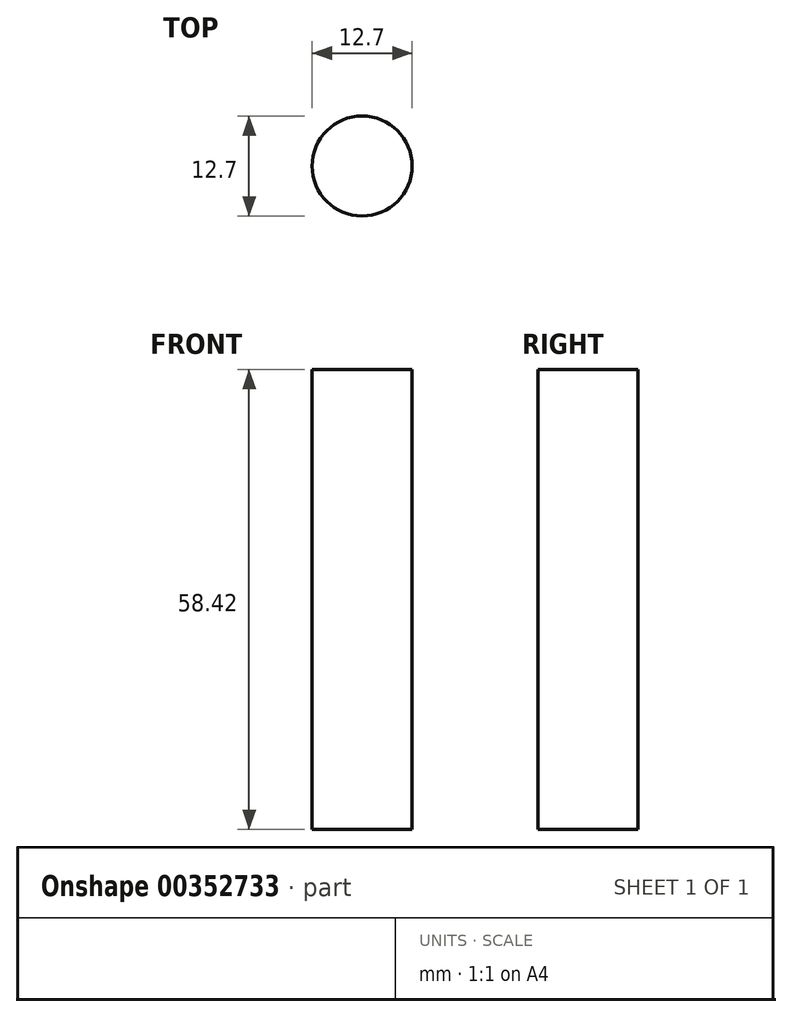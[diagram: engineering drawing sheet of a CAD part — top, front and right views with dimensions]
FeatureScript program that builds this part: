
annotation { "Feature Type Name" : "Feature", "Feature Type Description" : "" }
export const myFeature = defineFeature(function(context is Context, id is Id, definition is map)
    precondition{}
    {
        {
            var Q0;
            Q0=qCreatedBy(makeId("Front.planeOp"),FACE);
            var sketch = newSketch(context, id + "F0", { "sketchPlane" : qUnion([Q0])});
            skLineSegment(sketch, "E0.bottom", {"start": v(0, -17.78) * mm, "end": v(-6.35, -17.78) * mm});
            skLineSegment(sketch, "E0.top", {"start": v(0, -76.2) * mm, "end": v(-6.35, -76.2) * mm});
            skLineSegment(sketch, "E0.left", {"start": v(0, -17.78) * mm, "end": v(0, -76.2) * mm});
            skLineSegment(sketch, "E0.right", {"start": v(-6.35, -17.78) * mm, "end": v(-6.35, -76.2) * mm});
            skSolve(sketch);
        }
        {
            var Q0;
            Q0=makeQuery(id+"F0.imprint","IMPRINT",FACE,{"disambiguationData":[TD([[makeQuery(id+"F0.imprint","IMPRINT",EDGE,{"derivedFrom":sQuery(id+"F0.wireOp",EDGE,"E0.bottom")}),1.0]])]});
            var Q1;
            Q1=sQuery(id+"F0.wireOp",EDGE,"E0.left");
            revolve(context, id + "F1", {"entities" : qUnion([Q0]), "axis" : qUnion([Q1]), "revolveType" : RevolveType.FULL});
        }
    });
